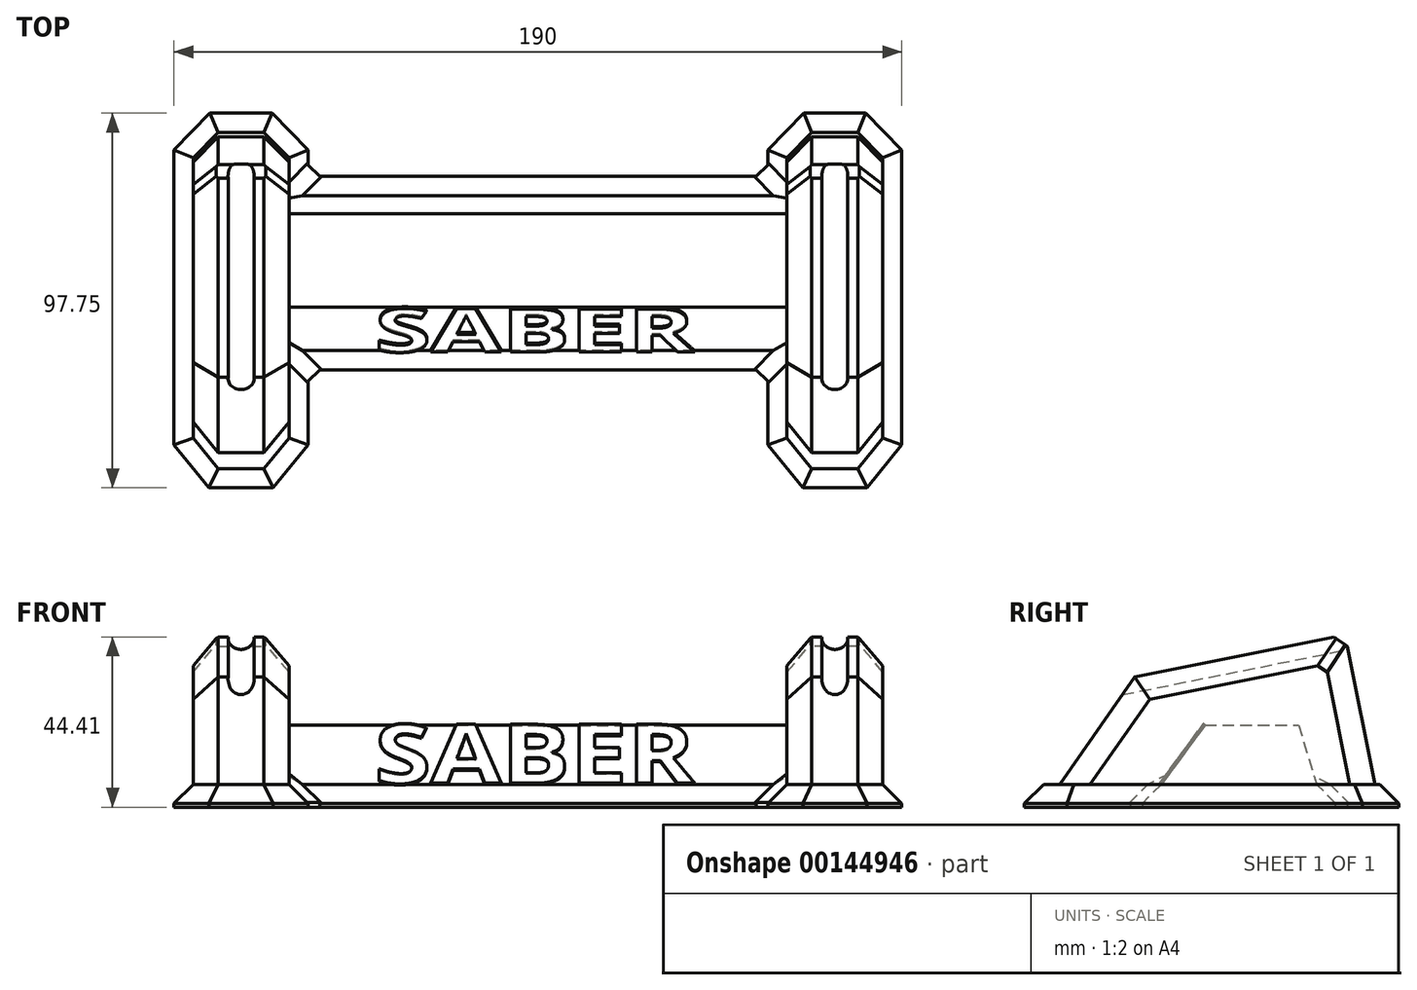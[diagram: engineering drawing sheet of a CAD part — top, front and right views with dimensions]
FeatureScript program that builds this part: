
annotation { "Feature Type Name" : "Feature", "Feature Type Description" : "" }
export const myFeature = defineFeature(function(context is Context, id is Id, definition is map)
    precondition{}
    {
        {
            var Q0;
            Q0=qCreatedBy(makeId("Right.planeOp"),FACE);
            var sketch = newSketch(context, id + "F0", { "sketchPlane" : qUnion([Q0])});
            skLineSegment(sketch, "E0", {"start": v(37.81, 0) * mm, "end": v(-49.94, 0) * mm});
            skLineSegment(sketch, "E1", {"start": v(-49.94, 0) * mm, "end": v(-26.11, 34) * mm});
            skLineSegment(sketch, "E2", {"start": v(-26.11, 34) * mm, "end": v(28.8, 45) * mm});
            skLineSegment(sketch, "E3", {"start": v(28.8, 45) * mm, "end": v(37.81, 0) * mm});
            skSolve(sketch);
        }
        {
            var Q0;
            Q0 = qSketchRegion(id + "F0", true);
            extrude(context, id + "F1", {"entities" : qUnion([Q0]), "depth" : 25 * mm, "symmetric" : true});
        }
        {
            var Q0;
            Q0=makeQuery(id+"F1.opExtrude","SWEPT_FACE",FACE,{"disambiguationData":[OSD([sQuery(id+"F0.wireOp",EDGE,"E3")])]});
            var sketch = newSketch(context, id + "F2", { "sketchPlane" : qUnion([Q0])});
            skCircle(sketch, "E4", {"center": v(0, 37.97) * mm, "radius": 3.4 * mm});
            skPoint(sketch, "E4.centerSnap0", {"position": v(0, 38.47) * mm});
            skSolve(sketch);
        }
        {
            var Q0;
            Q0 = qSketchRegion(id + "F2", true);
            extrude(context, id + "F3", {"entities" : qUnion([Q0]), "operationType" : NewBodyOperationType.REMOVE, "endBound" : BoundingType.THROUGH_ALL, "oppositeDirection" : true, "depth" : 25 * mm});
        }
        {
            var Q0;
            Q0=makeQuery(id+"F1.opExtrude","CAP_EDGE",EDGE,{"disambiguationData":[OSD([sQuery(id+"F0.wireOp",EDGE,"E2")])],"isStart":true});
            var Q1;
            Q1=makeQuery(id+"F1.opExtrude","CAP_EDGE",EDGE,{"disambiguationData":[OSD([sQuery(id+"F0.wireOp",EDGE,"E3")])],"isStart":true});
            var Q2;
            Q2=makeQuery(id+"F1.opExtrude","CAP_EDGE",EDGE,{"disambiguationData":[OSD([sQuery(id+"F0.wireOp",EDGE,"E3")])],"isStart":false});
            var Q3;
            Q3=makeQuery(id+"F1.opExtrude","CAP_EDGE",EDGE,{"disambiguationData":[OSD([sQuery(id+"F0.wireOp",EDGE,"E2")])],"isStart":false});
            var Q4;
            Q4=makeQuery(id+"F1.opExtrude","CAP_EDGE",EDGE,{"disambiguationData":[OSD([sQuery(id+"F0.wireOp",EDGE,"E1")])],"isStart":false});
            var Q5;
            Q5=makeQuery(id+"F1.opExtrude","CAP_EDGE",EDGE,{"disambiguationData":[OSD([sQuery(id+"F0.wireOp",EDGE,"E1")])],"isStart":true});
            chamfer(context, id + "F4", {"entities" : qUnion([Q0, Q1, Q2, Q3, Q4, Q5]), "width" : 6.5 * mm, "tangentPropagation" : true});
        }
        {
            var Q0;
            {var subQ0=sQuery(id+"F0.wireOp",EDGE,"E3");var subQ1=sQuery(id+"F0.wireOp",EDGE,"E2");Q0=makeQuery(id+"F3.boolean.opBoolean","SPLIT",EDGE,{"disambiguationData":[TD([makeQuery(id+"F1.opExtrude","CAP_FACE",FACE,{"disambiguationData":[OSD([sQuery(id+"F0.wireOp",EDGE,"E0"),sQuery(id+"F0.wireOp",EDGE,"E1"),subQ1,subQ0])],"isStart":false})])],"derivedFrom":makeQuery(id+"F1.opExtrude","SWEPT_EDGE",EDGE,{"disambiguationData":[OSD([subQ1,subQ0])]})});}
            var Q1;
            {var subQ0=sQuery(id+"F0.wireOp",EDGE,"E3");var subQ1=sQuery(id+"F0.wireOp",EDGE,"E2");Q1=makeQuery(id+"F3.boolean.opBoolean","SPLIT",EDGE,{"disambiguationData":[TD([makeQuery(id+"F1.opExtrude","CAP_FACE",FACE,{"disambiguationData":[OSD([sQuery(id+"F0.wireOp",EDGE,"E0"),sQuery(id+"F0.wireOp",EDGE,"E1"),subQ1,subQ0])],"isStart":true})])],"derivedFrom":makeQuery(id+"F1.opExtrude","SWEPT_EDGE",EDGE,{"disambiguationData":[OSD([subQ1,subQ0])]})});}
            var Q2;
            Q2=makeQuery(id+"F4.opChamfer","BLEND_EDGE",EDGE,{"blendedFrom":[makeQuery(id+"F1.opExtrude","CAP_EDGE",EDGE,{"disambiguationData":[OSD([sQuery(id+"F0.wireOp",EDGE,"E2")])],"isStart":true}),makeQuery(id+"F1.opExtrude","CAP_EDGE",EDGE,{"disambiguationData":[OSD([sQuery(id+"F0.wireOp",EDGE,"E3")])],"isStart":true})],"blendedInto":[]});
            var Q3;
            Q3=makeQuery(id+"F4.opChamfer","BLEND_EDGE",EDGE,{"blendedFrom":[makeQuery(id+"F1.opExtrude","CAP_EDGE",EDGE,{"disambiguationData":[OSD([sQuery(id+"F0.wireOp",EDGE,"E2")])],"isStart":false}),makeQuery(id+"F1.opExtrude","CAP_EDGE",EDGE,{"disambiguationData":[OSD([sQuery(id+"F0.wireOp",EDGE,"E3")])],"isStart":false})],"blendedInto":[]});
            chamfer(context, id + "F5", {"entities" : qUnion([Q0, Q1, Q2, Q3]), "width" : 3 * mm, "tangentPropagation" : true});
        }
        {
            var Q0;
            Q0=makeQuery(id+"F1.opExtrude","SWEPT_FACE",FACE,{"disambiguationData":[OSD([sQuery(id+"F0.wireOp",EDGE,"E0")])]});
            var sketch = newSketch(context, id + "F6", { "sketchPlane" : qUnion([Q0])});
            skLineSegment(sketch, "E5.0.0", {"start": v(6, 49.94) * mm, "end": v(-6, 49.94) * mm});
            skLineSegment(sketch, "E5.0.1", {"start": v(-6, 49.94) * mm, "end": v(-12.5, 42) * mm});
            skLineSegment(sketch, "E5.0.2", {"start": v(-12.5, 42) * mm, "end": v(-12.5, -31.18) * mm});
            skLineSegment(sketch, "E5.0.3", {"start": v(-12.5, -31.18) * mm, "end": v(-6, -37.81) * mm});
            skLineSegment(sketch, "E5.0.4", {"start": v(-6, -37.81) * mm, "end": v(6, -37.81) * mm});
            skLineSegment(sketch, "E5.0.5", {"start": v(6, -37.81) * mm, "end": v(12.5, -31.18) * mm});
            skLineSegment(sketch, "E5.0.6", {"start": v(12.5, -31.18) * mm, "end": v(12.5, 42) * mm});
            skLineSegment(sketch, "E5.0.7", {"start": v(12.5, 42) * mm, "end": v(6, 49.94) * mm});
            skLineSegment(sketch, "E6.0", {"start": v(-17.5, -33.22) * mm, "end": v(-8.1, -42.81) * mm});
            skLineSegment(sketch, "E6.1", {"start": v(-17.5, 43.8) * mm, "end": v(-17.5, -33.22) * mm});
            skLineSegment(sketch, "E6.2", {"start": v(-8.1, -42.81) * mm, "end": v(8.1, -42.81) * mm});
            skLineSegment(sketch, "E6.3", {"start": v(-8.37, 54.94) * mm, "end": v(-17.5, 43.8) * mm});
            skLineSegment(sketch, "E6.4", {"start": v(8.1, -42.81) * mm, "end": v(17.5, -33.22) * mm});
            skLineSegment(sketch, "E6.5", {"start": v(17.5, -33.22) * mm, "end": v(17.5, 43.8) * mm});
            skLineSegment(sketch, "E6.6", {"start": v(17.5, 43.8) * mm, "end": v(8.37, 54.94) * mm});
            skLineSegment(sketch, "E6.7", {"start": v(8.37, 54.94) * mm, "end": v(-8.37, 54.94) * mm});
            skSolve(sketch);
        }
        {
            var Q0;
            Q0=makeQuery(id+"F6.imprint","IMPRINT",FACE,{"disambiguationData":[TD([[makeQuery(id+"F6.imprint","IMPRINT",EDGE,{"derivedFrom":sQuery(id+"F6.wireOp",EDGE,"E5.0.0")}),-1.0]])]});
            var Q1;
            Q1=makeQuery(id+"F6.imprint","IMPRINT",FACE,{"disambiguationData":[TD([[makeQuery(id+"F6.imprint","IMPRINT",EDGE,{"derivedFrom":sQuery(id+"F6.wireOp",EDGE,"E5.0.0")}),1.0]])]});
            var Q2;
            Q2 = qConstructionFilter(qBodyType(qCreatedBy(id + "F6" ,EDGE), BodyType.WIRE), ConstructionObject.NO);
            extrude(context, id + "F7", {"entities" : qUnion([Q0, Q1]), "operationType" : NewBodyOperationType.ADD, "surfaceEntities" : qUnion([Q2]), "oppositeDirection" : true, "depth" : 6 * mm});
        }
        {
            var Q0;
            Q0=makeQuery(id+"F7.opExtrude","CAP_EDGE",EDGE,{"disambiguationData":[OSD([sQuery(id+"F6.wireOp",EDGE,"E6.3")])],"isStart":false});
            var Q1;
            Q1=makeQuery(id+"F7.opExtrude","CAP_EDGE",EDGE,{"disambiguationData":[OSD([sQuery(id+"F6.wireOp",EDGE,"E6.7")])],"isStart":false});
            var Q2;
            Q2=makeQuery(id+"F7.opExtrude","CAP_EDGE",EDGE,{"disambiguationData":[OSD([sQuery(id+"F6.wireOp",EDGE,"E6.1")])],"isStart":false});
            var Q3;
            Q3=makeQuery(id+"F7.opExtrude","CAP_EDGE",EDGE,{"disambiguationData":[OSD([sQuery(id+"F6.wireOp",EDGE,"E6.6")])],"isStart":false});
            var Q4;
            Q4=makeQuery(id+"F7.opExtrude","CAP_EDGE",EDGE,{"disambiguationData":[OSD([sQuery(id+"F6.wireOp",EDGE,"E6.5")])],"isStart":false});
            var Q5;
            Q5=makeQuery(id+"F7.opExtrude","CAP_EDGE",EDGE,{"disambiguationData":[OSD([sQuery(id+"F6.wireOp",EDGE,"E6.0")])],"isStart":false});
            var Q6;
            Q6=makeQuery(id+"F7.opExtrude","CAP_EDGE",EDGE,{"disambiguationData":[OSD([sQuery(id+"F6.wireOp",EDGE,"E6.2")])],"isStart":false});
            var Q7;
            Q7=makeQuery(id+"F7.opExtrude","CAP_EDGE",EDGE,{"disambiguationData":[OSD([sQuery(id+"F6.wireOp",EDGE,"E6.4")])],"isStart":false});
            chamfer(context, id + "F8", {"entities" : qUnion([Q0, Q1, Q2, Q3, Q4, Q5, Q6, Q7]), "width" : 5 * mm, "tangentPropagation" : true});
        }
        {
            var Q0;
            Q0=qCreatedBy(makeId("Right.planeOp"),FACE);
            cPlane(context, id + "F9", {"entities" : qUnion([Q0]), "cplaneType" : CPlaneType.OFFSET, "offset" : 77.5 * mm, "width" : 150 * mm, "height" : 150 * mm});
        }
        {
            var Q0;
            Q0=makeQuery(id+"F1.opExtrude","SWEPT_BODY",BODY,{"disambiguationData":[OSD([sQuery(id+"F0.wireOp",EDGE,"E0"),sQuery(id+"F0.wireOp",EDGE,"E1"),sQuery(id+"F0.wireOp",EDGE,"E2"),sQuery(id+"F0.wireOp",EDGE,"E3")])]});
            var Q1;
            Q1=qCreatedBy(id+"F9.planeOp",FACE);
            mirror(context, id + "F10", {"entities" : qUnion([Q0]), "mirrorPlane" : qUnion([Q1])});
        }
        {
            var Q0;
            Q0=qCreatedBy(id+"F9.planeOp",FACE);
            var sketch = newSketch(context, id + "F11", { "sketchPlane" : qUnion([Q0])});
            skLineSegment(sketch, "E7", {"start": v(-24.16, 0) * mm, "end": v(-24.16, 1) * mm});
            skLineSegment(sketch, "E8", {"start": v(-24.16, 1) * mm, "end": v(-19.16, 6) * mm});
            skLineSegment(sketch, "E9", {"start": v(-19.16, 6) * mm, "end": v(-7.81, 21.48) * mm});
            skLineSegment(sketch, "E10", {"start": v(-7.81, 21.48) * mm, "end": v(16.6, 21.48) * mm});
            skLineSegment(sketch, "E11", {"start": v(16.6, 21.48) * mm, "end": v(21.3, 6) * mm});
            skLineSegment(sketch, "E12", {"start": v(21.3, 6) * mm, "end": v(26.3, 1) * mm});
            skLineSegment(sketch, "E13", {"start": v(26.3, 1) * mm, "end": v(26.3, 0) * mm});
            skLineSegment(sketch, "E14", {"start": v(26.3, 0) * mm, "end": v(-24.16, 0) * mm});
            skSolve(sketch);
        }
        {
            var Q0;
            Q0 = qSketchRegion(id + "F11", true);
            var Q1;
            Q1=makeQuery(id+"F10.opPattern","COPY",FACE,{"derivedFrom":makeQuery(id+"F1.opExtrude","CAP_FACE",FACE,{"disambiguationData":[OSD([sQuery(id+"F0.wireOp",EDGE,"E0"),sQuery(id+"F0.wireOp",EDGE,"E1"),sQuery(id+"F0.wireOp",EDGE,"E2"),sQuery(id+"F0.wireOp",EDGE,"E3")])],"isStart":false}),"instanceName":"1"});
            var Q2;
            Q2=makeQuery(id+"F1.opExtrude","CAP_FACE",FACE,{"disambiguationData":[OSD([sQuery(id+"F0.wireOp",EDGE,"E0"),sQuery(id+"F0.wireOp",EDGE,"E1"),sQuery(id+"F0.wireOp",EDGE,"E2"),sQuery(id+"F0.wireOp",EDGE,"E3")])],"isStart":false});
            extrude(context, id + "F12", {"entities" : qUnion([Q0]), "operationType" : NewBodyOperationType.ADD, "endBound" : BoundingType.UP_TO_SURFACE, "endBoundEntityFace" : qUnion([Q1]), "depth" : 25 * mm, "hasSecondDirection" : true, "secondDirectionBound" : BoundingType.UP_TO_SURFACE, "secondDirectionOppositeDirection" : true, "secondDirectionBoundEntityFace" : qUnion([Q2]), "secondDirectionDepth" : 25 * mm});
        }
        {
            var Q0;
            Q0=makeQuery(id+"F12.opExtrude","TWEAK_EDGE",EDGE,{"derivedFrom":[makeQuery(id+"F1.opExtrude","CAP_FACE",FACE,{"disambiguationData":[OSD([sQuery(id+"F0.wireOp",EDGE,"E0"),sQuery(id+"F0.wireOp",EDGE,"E1"),sQuery(id+"F0.wireOp",EDGE,"E2"),sQuery(id+"F0.wireOp",EDGE,"E3")])],"isStart":false}),makeQuery(id+"F11.imprint","IMPRINT",EDGE,{"derivedFrom":sQuery(id+"F11.wireOp",EDGE,"E9")})]});
            var Q1;
            Q1=makeQuery(id+"F12.opExtrude","TWEAK_EDGE",EDGE,{"derivedFrom":[makeQuery(id+"F1.opExtrude","CAP_FACE",FACE,{"disambiguationData":[OSD([sQuery(id+"F0.wireOp",EDGE,"E0"),sQuery(id+"F0.wireOp",EDGE,"E1"),sQuery(id+"F0.wireOp",EDGE,"E2"),sQuery(id+"F0.wireOp",EDGE,"E3")])],"isStart":false}),makeQuery(id+"F11.imprint","IMPRINT",EDGE,{"derivedFrom":sQuery(id+"F11.wireOp",EDGE,"E10")})]});
            var Q2;
            Q2=makeQuery(id+"F12.boolean.opBoolean","INTERSECT",EDGE,{"derivedFrom":[makeQuery(id+"F8.opChamfer","BLEND_FACE",FACE,{"disambiguationData":[OSD([sQuery(id+"F6.wireOp",EDGE,"E6.5")])]}),makeQuery(id+"F12.opExtrude","SWEPT_FACE",FACE,{"disambiguationData":[OSD([sQuery(id+"F11.wireOp",EDGE,"E8")])]})]});
            var Q3;
            Q3=makeQuery(id+"F12.boolean.opBoolean","INTERSECT",EDGE,{"derivedFrom":[makeQuery(id+"F10.opPattern","COPY",FACE,{"derivedFrom":makeQuery(id+"F8.opChamfer","BLEND_FACE",FACE,{"disambiguationData":[OSD([sQuery(id+"F6.wireOp",EDGE,"E6.5")])]}),"instanceName":"1"}),makeQuery(id+"F12.opExtrude","SWEPT_FACE",FACE,{"disambiguationData":[OSD([sQuery(id+"F11.wireOp",EDGE,"E8")])]})]});
            var Q4;
            Q4=makeQuery(id+"F12.opExtrude","TWEAK_EDGE",EDGE,{"derivedFrom":[makeQuery(id+"F10.opPattern","COPY",FACE,{"derivedFrom":makeQuery(id+"F1.opExtrude","CAP_FACE",FACE,{"disambiguationData":[OSD([sQuery(id+"F0.wireOp",EDGE,"E0"),sQuery(id+"F0.wireOp",EDGE,"E1"),sQuery(id+"F0.wireOp",EDGE,"E2"),sQuery(id+"F0.wireOp",EDGE,"E3")])],"isStart":false}),"instanceName":"1"}),makeQuery(id+"F11.imprint","IMPRINT",EDGE,{"derivedFrom":sQuery(id+"F11.wireOp",EDGE,"E9")})]});
            var Q5;
            Q5=makeQuery(id+"F12.opExtrude","TWEAK_EDGE",EDGE,{"derivedFrom":[makeQuery(id+"F10.opPattern","COPY",FACE,{"derivedFrom":makeQuery(id+"F1.opExtrude","CAP_FACE",FACE,{"disambiguationData":[OSD([sQuery(id+"F0.wireOp",EDGE,"E0"),sQuery(id+"F0.wireOp",EDGE,"E1"),sQuery(id+"F0.wireOp",EDGE,"E2"),sQuery(id+"F0.wireOp",EDGE,"E3")])],"isStart":false}),"instanceName":"1"}),makeQuery(id+"F11.imprint","IMPRINT",EDGE,{"derivedFrom":sQuery(id+"F11.wireOp",EDGE,"E10")})]});
            var Q6;
            Q6=makeQuery(id+"F12.opExtrude","TWEAK_EDGE",EDGE,{"derivedFrom":[makeQuery(id+"F10.opPattern","COPY",FACE,{"derivedFrom":makeQuery(id+"F1.opExtrude","CAP_FACE",FACE,{"disambiguationData":[OSD([sQuery(id+"F0.wireOp",EDGE,"E0"),sQuery(id+"F0.wireOp",EDGE,"E1"),sQuery(id+"F0.wireOp",EDGE,"E2"),sQuery(id+"F0.wireOp",EDGE,"E3")])],"isStart":false}),"instanceName":"1"}),makeQuery(id+"F11.imprint","IMPRINT",EDGE,{"derivedFrom":sQuery(id+"F11.wireOp",EDGE,"E11")})]});
            var Q7;
            Q7=makeQuery(id+"F12.boolean.opBoolean","INTERSECT",EDGE,{"derivedFrom":[makeQuery(id+"F10.opPattern","COPY",FACE,{"derivedFrom":makeQuery(id+"F8.opChamfer","BLEND_FACE",FACE,{"disambiguationData":[OSD([sQuery(id+"F6.wireOp",EDGE,"E6.5")])]}),"instanceName":"1"}),makeQuery(id+"F12.opExtrude","SWEPT_FACE",FACE,{"disambiguationData":[OSD([sQuery(id+"F11.wireOp",EDGE,"E12")])]})]});
            var Q8;
            Q8=makeQuery(id+"F12.opExtrude","TWEAK_EDGE",EDGE,{"derivedFrom":[makeQuery(id+"F1.opExtrude","CAP_FACE",FACE,{"disambiguationData":[OSD([sQuery(id+"F0.wireOp",EDGE,"E0"),sQuery(id+"F0.wireOp",EDGE,"E1"),sQuery(id+"F0.wireOp",EDGE,"E2"),sQuery(id+"F0.wireOp",EDGE,"E3")])],"isStart":false}),makeQuery(id+"F11.imprint","IMPRINT",EDGE,{"derivedFrom":sQuery(id+"F11.wireOp",EDGE,"E11")})]});
            var Q9;
            Q9=makeQuery(id+"F12.boolean.opBoolean","INTERSECT",EDGE,{"derivedFrom":[makeQuery(id+"F8.opChamfer","BLEND_FACE",FACE,{"disambiguationData":[OSD([sQuery(id+"F6.wireOp",EDGE,"E6.5")])]}),makeQuery(id+"F12.opExtrude","SWEPT_FACE",FACE,{"disambiguationData":[OSD([sQuery(id+"F11.wireOp",EDGE,"E12")])]})]});
            chamfer(context, id + "F13", {"entities" : qUnion([Q0, Q1, Q2, Q3, Q4, Q5, Q6, Q7, Q8, Q9]), "width" : 5 * mm, "tangentPropagation" : true});
        }
        {
            var Q0;
            Q0=makeQuery(id+"F12.boolean.opBoolean","INTERSECT",EDGE,{"derivedFrom":[makeQuery(id+"F7.opExtrude","SWEPT_FACE",FACE,{"disambiguationData":[OSD([sQuery(id+"F6.wireOp",EDGE,"E6.5")])]}),makeQuery(id+"F12.opExtrude","SWEPT_FACE",FACE,{"disambiguationData":[OSD([sQuery(id+"F11.wireOp",EDGE,"E7")])]})]});
            var Q1;
            Q1=makeQuery(id+"F12.boolean.opBoolean","INTERSECT",EDGE,{"derivedFrom":[makeQuery(id+"F10.opPattern","COPY",FACE,{"derivedFrom":makeQuery(id+"F7.opExtrude","SWEPT_FACE",FACE,{"disambiguationData":[OSD([sQuery(id+"F6.wireOp",EDGE,"E6.5")])]}),"instanceName":"1"}),makeQuery(id+"F12.opExtrude","SWEPT_FACE",FACE,{"disambiguationData":[OSD([sQuery(id+"F11.wireOp",EDGE,"E7")])]})]});
            var Q2;
            Q2=makeQuery(id+"F12.boolean.opBoolean","INTERSECT",EDGE,{"derivedFrom":[makeQuery(id+"F10.opPattern","COPY",FACE,{"derivedFrom":makeQuery(id+"F7.opExtrude","SWEPT_FACE",FACE,{"disambiguationData":[OSD([sQuery(id+"F6.wireOp",EDGE,"E6.5")])]}),"instanceName":"1"}),makeQuery(id+"F12.opExtrude","SWEPT_FACE",FACE,{"disambiguationData":[OSD([sQuery(id+"F11.wireOp",EDGE,"E13")])]})]});
            var Q3;
            Q3=makeQuery(id+"F12.boolean.opBoolean","INTERSECT",EDGE,{"derivedFrom":[makeQuery(id+"F7.opExtrude","SWEPT_FACE",FACE,{"disambiguationData":[OSD([sQuery(id+"F6.wireOp",EDGE,"E6.5")])]}),makeQuery(id+"F12.opExtrude","SWEPT_FACE",FACE,{"disambiguationData":[OSD([sQuery(id+"F11.wireOp",EDGE,"E13")])]})]});
            chamfer(context, id + "F14", {"entities" : qUnion([Q0, Q1, Q2, Q3]), "width" : 3 * mm, "tangentPropagation" : true});
        }
        {
            var Q0;
            Q0=makeQuery(id+"F12.opExtrude","SWEPT_FACE",FACE,{"disambiguationData":[OSD([sQuery(id+"F11.wireOp",EDGE,"E9")])]});
            var sketch = newSketch(context, id + "F15", { "sketchPlane" : qUnion([Q0])});
            skText(sketch, "E15", { "text": "SABER", "fontName": "OpenSans-Bold.ttf"});
            skPoint(sketch, "E16", {"position": v(77.5, 12.7) * mm});
            const initialGuessF15  = {"E15": [0.03488, -0.00649, 1, 0, 0.0192]};
            skSetInitialGuess(sketch, initialGuessF15);
            skSolve(sketch);
        }
        {
            var Q0;
            Q0 = qSketchRegion(id + "F15", true);
            extrude(context, id + "F16", {"entities" : qUnion([Q0]), "operationType" : NewBodyOperationType.ADD, "depth" : .5 * mm});
        }
    });
